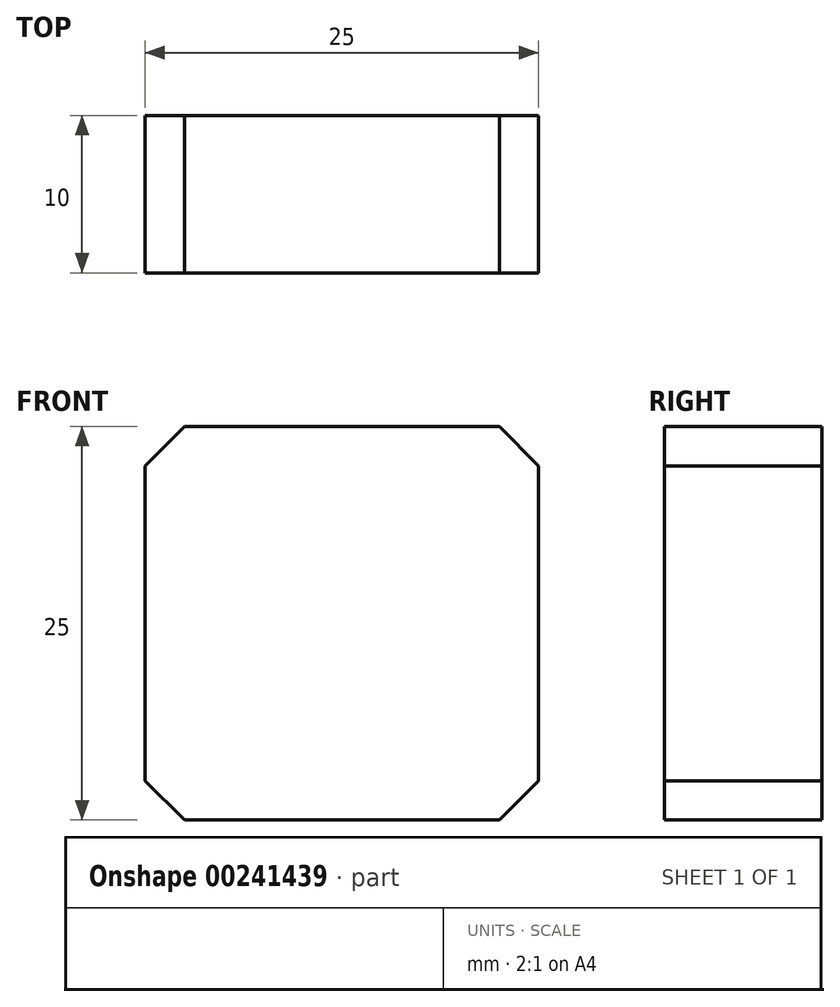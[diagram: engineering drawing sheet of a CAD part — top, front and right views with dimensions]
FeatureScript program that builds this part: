
annotation { "Feature Type Name" : "Feature", "Feature Type Description" : "" }
export const myFeature = defineFeature(function(context is Context, id is Id, definition is map)
    precondition{}
    {
        {
            var Q0;
            Q0=qCreatedBy(makeId("Front.planeOp"),FACE);
            var sketch = newSketch(context, id + "F0", { "sketchPlane" : qUnion([Q0])});
            skLineSegment(sketch, "E0.bottom", {"start": v(-12.5, 12.5) * mm, "end": v(12.5, 12.5) * mm});
            skLineSegment(sketch, "E0.top", {"start": v(-12.5, -12.5) * mm, "end": v(12.5, -12.5) * mm});
            skLineSegment(sketch, "E0.left", {"start": v(-12.5, 12.5) * mm, "end": v(-12.5, -12.5) * mm});
            skLineSegment(sketch, "E0.right", {"start": v(12.5, 12.5) * mm, "end": v(12.5, -12.5) * mm});
            skPoint(sketch, "E0.middle", {"position": v(0, 0) * mm});
            skSolve(sketch);
        }
        {
            var Q0;
            Q0 = qSketchRegion(id + "F0", true);
            extrude(context, id + "F1", {"entities" : qUnion([Q0]), "depth" : 10 * mm});
        }
        {
            var Q0;
            Q0=makeQuery(id+"F1.opExtrude","SWEPT_EDGE",EDGE,{"disambiguationData":[OSD([sQuery(id+"F0.wireOp",EDGE,"E0.bottom"),sQuery(id+"F0.wireOp",EDGE,"E0.left")])]});
            var Q1;
            Q1=makeQuery(id+"F1.opExtrude","SWEPT_EDGE",EDGE,{"disambiguationData":[OSD([sQuery(id+"F0.wireOp",EDGE,"E0.bottom"),sQuery(id+"F0.wireOp",EDGE,"E0.right")])]});
            var Q2;
            Q2=makeQuery(id+"F1.opExtrude","SWEPT_EDGE",EDGE,{"disambiguationData":[OSD([sQuery(id+"F0.wireOp",EDGE,"E0.top"),sQuery(id+"F0.wireOp",EDGE,"E0.left")])]});
            var Q3;
            Q3=makeQuery(id+"F1.opExtrude","SWEPT_EDGE",EDGE,{"disambiguationData":[OSD([sQuery(id+"F0.wireOp",EDGE,"E0.top"),sQuery(id+"F0.wireOp",EDGE,"E0.right")])]});
            chamfer(context, id + "F2", {"entities" : qUnion([Q0, Q1, Q2, Q3]), "width" : 2.5 * mm});
        }
    });
